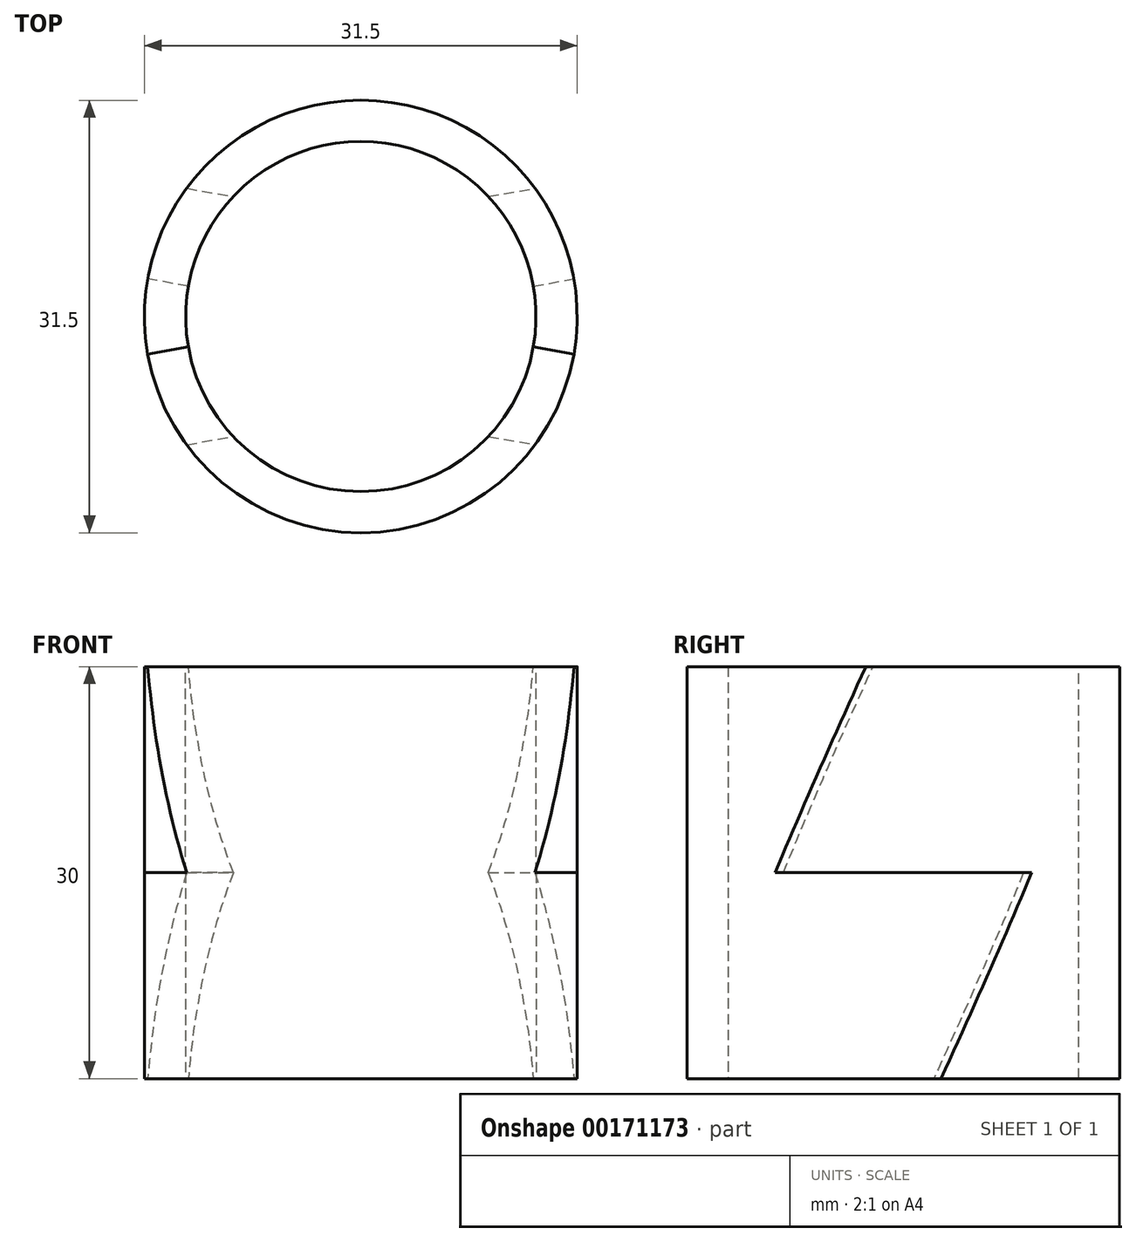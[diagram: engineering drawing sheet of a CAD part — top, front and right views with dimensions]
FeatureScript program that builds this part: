
annotation { "Feature Type Name" : "Feature", "Feature Type Description" : "" }
export const myFeature = defineFeature(function(context is Context, id is Id, definition is map)
    precondition{}
    {
        {
            assignVariable(context, id + "F0", {"name" : "Height", "anyValue" : 15});
        }
        {
            assignVariable(context, id + "F1", {"name" : "Angle2", "anyValue" : 25});
        }
        {
            var Q0;
            Q0=qCreatedBy(makeId("Top.planeOp"),FACE);
            var sketch = newSketch(context, id + "F2", { "sketchPlane" : qUnion([Q0])});
            skArc(sketch, "E0", {"start": v(-12.56, -2.21) * mm, "mid": v(0, 12.75) * mm, "end": v(12.56, -2.21) * mm});
            skLineSegment(sketch, "E1", {"start": v(0, 0) * mm, "end": v(-12.56, -2.21) * mm, "construction": true});
            skLineSegment(sketch, "E2", {"start": v(0, 0) * mm, "end": v(12.56, -2.21) * mm, "construction": true});
            skLineSegment(sketch, "E3", {"start": v(-12.56, -2.21) * mm, "end": v(-15.51, -2.73) * mm});
            skLineSegment(sketch, "E4", {"start": v(12.56, -2.21) * mm, "end": v(15.51, -2.73) * mm});
            skArc(sketch, "E5", {"start": v(-15.51, -2.73) * mm, "mid": v(0, 15.75) * mm, "end": v(15.51, -2.73) * mm});
            skLineSegment(sketch, "E6", {"start": v(0, 0) * mm, "end": v(-12.56, 2.21) * mm, "construction": true});
            skLineSegment(sketch, "E7", {"start": v(0, 0) * mm, "end": v(12.56, 2.21) * mm, "construction": true});
            skLineSegment(sketch, "E8", {"start": v(-12.56, 2.21) * mm, "end": v(-15.51, 2.73) * mm});
            skLineSegment(sketch, "E9", {"start": v(12.56, 2.21) * mm, "end": v(15.51, 2.73) * mm});
            skArc(sketch, "E10", {"start": v(-12.56, -2.21) * mm, "mid": v(0, -12.75) * mm, "end": v(12.56, -2.21) * mm});
            skArc(sketch, "E11", {"start": v(-15.51, -2.73) * mm, "mid": v(0, -15.75) * mm, "end": v(15.51, -2.73) * mm});
            skLineSegment(sketch, "E12", {"start": v(0, 0) * mm, "end": v(0, -26.95) * mm, "construction": true});
            skSolve(sketch);
        }
        {
            var Q0;
            {var subQ0=sQuery(id+"F2.wireOp",EDGE,"E4");Q0=makeQuery(id+"F2.imprint","IMPRINT",FACE,{"disambiguationData":[TD([[makeQuery(id+"F2.imprint","IMPRINT",EDGE,{"derivedFrom":subQ0}),1.0]])]});}
            var Q1;
            Q1=makeQuery(id+"F2.imprint","IMPRINT",FACE,{"disambiguationData":[TD([[makeQuery(id+"F2.imprint","IMPRINT",EDGE,{"derivedFrom":sQuery(id+"F2.wireOp",EDGE,"E3")}),1.0]])]});
            var Q2;
            {var subQ0=sQuery(id+"F2.wireOp",EDGE,"E3");Q2=makeQuery(id+"F2.imprint","IMPRINT",FACE,{"disambiguationData":[TD([[makeQuery(id+"F2.imprint","IMPRINT",EDGE,{"derivedFrom":subQ0}),-1.0]])]});}
            var Q3;
            {var subQ0=sQuery(id+"F2.wireOp",EDGE,"E8");Q3=makeQuery(id+"F2.imprint","IMPRINT",FACE,{"disambiguationData":[TD([[makeQuery(id+"F2.imprint","IMPRINT",EDGE,{"derivedFrom":subQ0}),-1.0]])]});}
            extrude(context, id + "F3", {"entities" : qUnion([Q0, Q1, Q2, Q3]), "depth" : getVariable(context, 'Height') * mm});
        }
        {
            var Q0;
            {var subQ0=sQuery(id+"F2.wireOp",EDGE,"E8");Q0=makeQuery(id+"F2.imprint","IMPRINT",FACE,{"disambiguationData":[TD([[makeQuery(id+"F2.imprint","IMPRINT",EDGE,{"derivedFrom":subQ0}),-1.0]])]});}
            extrude(context, id + "F4", {"entities" : qUnion([Q0]), "oppositeDirection" : true, "depth" : getVariable(context, 'Height') * mm});
        }
        {
            var Q0;
            Q0=makeQuery(id+"F4.opExtrude","CAP_EDGE",EDGE,{"disambiguationData":[OSD([sQuery(id+"F2.wireOp",EDGE,"E8")])],"isStart":false});
            var Q1;
            Q1=makeQuery(id+"F4.opExtrude","CAP_EDGE",EDGE,{"disambiguationData":[OSD([sQuery(id+"F2.wireOp",EDGE,"E9")])],"isStart":false});
            chamfer(context, id + "F5", {"entities" : qUnion([Q0, Q1]), "chamferType" : ChamferType.TWO_OFFSETS, "width1" : getVariable(context, 'Height') * tan(getVariable(context, 'Angle2') * degree) * mm, "oppositeDirection" : false, "width2" : getVariable(context, 'Height') * mm, "tangentPropagation" : true});
        }
        {
            var Q0;
            Q0=makeQuery(id+"F4.opExtrude","SWEPT_BODY",BODY,{"disambiguationData":[OSD([sQuery(id+"F2.wireOp",EDGE,"E0"),sQuery(id+"F2.wireOp",EDGE,"E5"),sQuery(id+"F2.wireOp",EDGE,"E8"),sQuery(id+"F2.wireOp",EDGE,"E9")])]});
            var Q1;
            Q1=sQuery(id+"F2.wireOp",EDGE,"E12");
            transform(context, id + "F6", {"entities" : qUnion([Q0]), "transformType" : TransformType.ROTATION, "transformAxis" : qUnion([Q1]), "angle" : 180 * degree, "makeCopy" : false});
        }
        {
            var Q0;
            Q0=makeQuery(id+"F4.opExtrude","SWEPT_BODY",BODY,{"disambiguationData":[OSD([sQuery(id+"F2.wireOp",EDGE,"E0"),sQuery(id+"F2.wireOp",EDGE,"E5"),sQuery(id+"F2.wireOp",EDGE,"E8"),sQuery(id+"F2.wireOp",EDGE,"E9")])]});
            var Q1;
            Q1=makeQuery(id+"F3.opExtrude","SWEPT_BODY",BODY,{"disambiguationData":[OSD([sQuery(id+"F2.wireOp",EDGE,"E0"),sQuery(id+"F2.wireOp",EDGE,"E5"),sQuery(id+"F2.wireOp",EDGE,"E10"),sQuery(id+"F2.wireOp",EDGE,"E11")])]});
            booleanBodies(context, id + "F7", {"operationType" : BooleanOperationType.SUBTRACTION, "tools" : qUnion([Q0]), "targets" : qUnion([Q1]), "keepTools" : true});
        }
        {
            var Q0;
            Q0=makeQuery(id+"F3.opExtrude","CAP_FACE",FACE,{"disambiguationData":[OSD([sQuery(id+"F2.wireOp",EDGE,"E0"),sQuery(id+"F2.wireOp",EDGE,"E5"),sQuery(id+"F2.wireOp",EDGE,"E10"),sQuery(id+"F2.wireOp",EDGE,"E11")])],"isStart":false});
            var sketch = newSketch(context, id + "F8", { "sketchPlane" : qUnion([Q0])});
            skLineSegment(sketch, "E13", {"start": v(0, 0) * mm, "end": v(-27.45, 0) * mm, "construction": true});
            skSolve(sketch);
        }
        {
            var Q0;
            Q0=makeQuery(id+"F4.opExtrude","SWEPT_BODY",BODY,{"disambiguationData":[OSD([sQuery(id+"F2.wireOp",EDGE,"E0"),sQuery(id+"F2.wireOp",EDGE,"E5"),sQuery(id+"F2.wireOp",EDGE,"E8"),sQuery(id+"F2.wireOp",EDGE,"E9")])]});
            var Q1;
            Q1=sQuery(id+"F8.wireOp",EDGE,"E13");
            transform(context, id + "F9", {"entities" : qUnion([Q0]), "transformType" : TransformType.ROTATION, "transformAxis" : qUnion([Q1]), "angle" : 180 * degree, "makeCopy" : false});
        }
        {
            var Q0;
            Q0=makeQuery(id+"F3.opExtrude","SWEPT_BODY",BODY,{"disambiguationData":[OSD([sQuery(id+"F2.wireOp",EDGE,"E0"),sQuery(id+"F2.wireOp",EDGE,"E5"),sQuery(id+"F2.wireOp",EDGE,"E10"),sQuery(id+"F2.wireOp",EDGE,"E11")])]});
            var Q1;
            Q1=makeQuery(id+"F4.opExtrude","SWEPT_BODY",BODY,{"disambiguationData":[OSD([sQuery(id+"F2.wireOp",EDGE,"E0"),sQuery(id+"F2.wireOp",EDGE,"E5"),sQuery(id+"F2.wireOp",EDGE,"E8"),sQuery(id+"F2.wireOp",EDGE,"E9")])]});
            booleanBodies(context, id + "F10", {"operationType" : BooleanOperationType.UNION, "tools" : qUnion([Q0, Q1])});
        }
        {
            var Q0;
            Q0=makeQuery(id+"F3.opExtrude","SWEPT_BODY",BODY,{"disambiguationData":[OSD([sQuery(id+"F2.wireOp",EDGE,"E0"),sQuery(id+"F2.wireOp",EDGE,"E5"),sQuery(id+"F2.wireOp",EDGE,"E10"),sQuery(id+"F2.wireOp",EDGE,"E11")])]});
            var Q1;
            Q1=sQuery(id+"F8.wireOp",EDGE,"E13");
            transform(context, id + "F11", {"entities" : qUnion([Q0]), "transformType" : TransformType.ROTATION, "transformAxis" : qUnion([Q1]), "angle" : 180 * degree, "makeCopy" : true});
        }
    });
